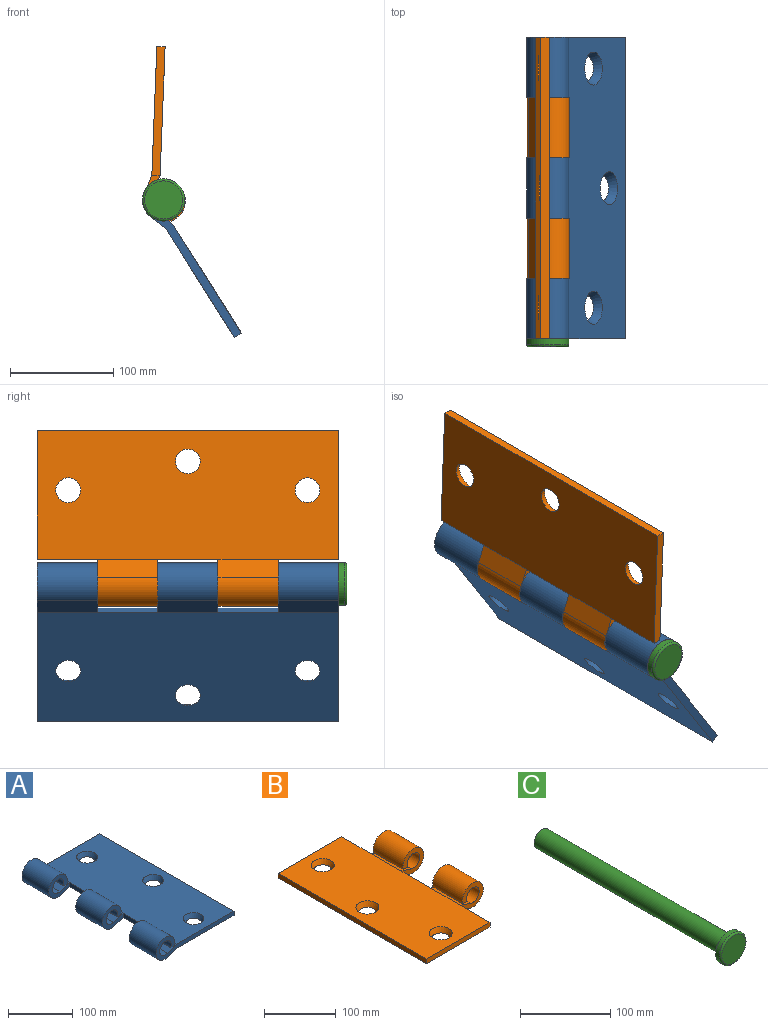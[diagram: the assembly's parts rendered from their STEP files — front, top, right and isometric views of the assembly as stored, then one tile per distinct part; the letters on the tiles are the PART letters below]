
ASSEMBLY  parts=3 mates=2
PART A: 29 faces, bbox 170x292x41 mm
  f0: cylinder r=12.5mm len=58.4mm, axis (0,1,0), area 3975.6mm2, adj f2,f8,f24,f28
  f1: cylinder r=12.5mm len=58.4mm, axis (0,1,0), area 3975.6mm2, adj f3,f9,f18,f25
  f2: plane 58.4x20.54mm, normal (-0.32,0,0.95), area 1264.7mm2, adj f0,f12,f24,f28
  f3: plane 58.4x20.54mm, normal (-0.32,0,0.95), area 1264.7mm2, adj f1,f12,f18,f25
  f4: plane 58.4x17.59mm, normal (0.34,0,-0.94), area 1091mm2, adj f6,f14,f24,f28
  f5: plane 58.4x17.59mm, normal (0.34,0,-0.94), area 1091mm2, adj f7,f14,f18,f25
  f6: cylinder r=20.5mm len=58.4mm, axis (0,1,0), area 6348.4mm2, adj f4,f8,f24,f28
  f7: cylinder r=20.5mm len=58.4mm, axis (0,1,0), area 6348.4mm2, adj f5,f9,f18,f25
  f8: plane 58.4x8.42mm, normal (0,0,-1), area 492mm2, adj f0,f6,f24,f28
  f9: plane 58.4x8.42mm, normal (0,0,-1), area 492mm2, adj f1,f7,f18,f25
  f10: cylinder r=12.5mm len=58.4mm, axis (0,1,0), area 3975.6mm2, adj f11,f17,f19,f27
  f11: plane 58.4x20.54mm, normal (-0.32,0,0.95), area 1264.7mm2, adj f10,f12,f19,f27
  f12: plane 292x125mm, normal (0,0,1), area 34087.3mm2, adj f2,f3,f11,f13,f18,f19,f20,f21
  f13: plane 292x8mm, normal (1,0,0), area 2336mm2, adj f12,f14,f18,f19
  f14: plane 292x125mm, normal (0,0,-1), area 35142.8mm2, adj f4,f5,f13,f15,f18,f19,f20,f21
  f15: plane 58.4x17.59mm, normal (0.34,0,-0.94), area 1091mm2, adj f14,f16,f19,f27
  f16: cylinder r=20.5mm len=58.4mm, axis (0,1,0), area 6348.4mm2, adj f15,f17,f19,f27
  f17: plane 58.4x8.42mm, normal (0,0,-1), area 492mm2, adj f10,f16,f19,f27
  f18: plane 170x41mm, normal (0,-1,0), area 1864mm2, adj f1,f3,f5,f7,f9,f12,f13,f14
  f19: plane 170x41mm, normal (0,1,0), area 1864mm2, adj f10,f11,f12,f13,f14,f15,f16,f17
  f20: cone r=12mm half-angle=26.6deg, axis (0,0,1), area 786.8mm2, adj f12,f14
  f21: cone r=12mm half-angle=26.6deg, axis (0,0,1), area 786.8mm2, adj f12,f14
  f22: cone r=12mm half-angle=26.6deg, axis (0,0,1), area 786.8mm2, adj f12,f14
  f23: plane 58.4x8mm, normal (-1,0,0), area 467.2mm2, adj f12,f14,f24,f25
  f24: plane 45x41mm, normal (0,-1,0), area 864mm2, adj f0,f2,f4,f6,f8,f23
  f25: plane 45x41mm, normal (0,1,0), area 864mm2, adj f1,f3,f5,f7,f9,f23
  f26: plane 58.4x8mm, normal (-1,0,0), area 467.2mm2, adj f12,f14,f27,f28
  f27: plane 45x41mm, normal (0,-1,0), area 864mm2, adj f10,f11,f15,f16,f17,f26
  f28: plane 45x41mm, normal (0,1,0), area 864mm2, adj f0,f2,f4,f6,f8,f26
PART B: 25 faces, bbox 170x292x41 mm
  f0: cylinder r=12.5mm len=58.4mm, axis (0,1,0), area 3975.6mm2, adj f2,f8,f21,f24
  f1: cylinder r=12.5mm len=58.4mm, axis (0,1,0), area 3975.6mm2, adj f3,f9,f19,f22
  f2: plane 58.4x20.54mm, normal (0.32,0,0.95), area 1264.7mm2, adj f0,f12,f21,f24
  f3: plane 58.4x20.54mm, normal (0.32,0,0.95), area 1264.7mm2, adj f1,f12,f19,f22
  f4: plane 58.4x17.59mm, normal (-0.34,0,-0.94), area 1091mm2, adj f6,f14,f21,f24
  f5: plane 58.4x17.59mm, normal (-0.34,0,-0.94), area 1091mm2, adj f7,f14,f19,f22
  f6: cylinder r=20.5mm len=58.4mm, axis (0,1,0), area 6348.4mm2, adj f4,f8,f21,f24
  f7: cylinder r=20.5mm len=58.4mm, axis (0,1,0), area 6348.4mm2, adj f5,f9,f19,f22
  f8: plane 58.4x8.42mm, normal (0,0,-1), area 492mm2, adj f0,f6,f21,f24
  f9: plane 58.4x8.42mm, normal (0,0,-1), area 492mm2, adj f1,f7,f19,f22
  f10: plane 125x8mm, normal (0,-1,0), area 1000mm2, adj f12,f13,f14,f18
  f11: plane 125x8mm, normal (0,1,0), area 1000mm2, adj f12,f13,f14,f23
  f12: plane 292x125mm, normal (0,0,1), area 34087.3mm2, adj f2,f3,f10,f11,f13,f15,f16,f17
  f13: plane 292x8mm, normal (-1,0,0), area 2336mm2, adj f10,f11,f12,f14
  f14: plane 292x125mm, normal (0,0,-1), area 35142.8mm2, adj f4,f5,f10,f11,f13,f15,f16,f17
  f15: cone r=12mm half-angle=26.6deg, axis (0,0,1), area 786.8mm2, adj f12,f14
  f16: cone r=12mm half-angle=26.6deg, axis (0,0,1), area 786.8mm2, adj f12,f14
  f17: cone r=12mm half-angle=26.6deg, axis (0,0,1), area 786.8mm2, adj f12,f14
  f18: plane 58.4x8mm, normal (1,0,0), area 467.2mm2, adj f10,f12,f14,f19
  f19: plane 45x41mm, normal (0,-1,0), area 864mm2, adj f1,f3,f5,f7,f9,f18
  f20: plane 58.4x8mm, normal (1,0,0), area 467.2mm2, adj f12,f14,f21,f22
  f21: plane 45x41mm, normal (0,-1,0), area 864mm2, adj f0,f2,f4,f6,f8,f20
  f22: plane 45x41mm, normal (0,1,0), area 864mm2, adj f1,f3,f5,f7,f9,f20
  f23: plane 58.4x8mm, normal (1,0,0), area 467.2mm2, adj f11,f12,f14,f24
  f24: plane 45x41mm, normal (0,1,0), area 864mm2, adj f0,f2,f4,f6,f8,f23
PART C: 6 faces, bbox 44.4x300x44.4 mm
  f0: cylinder r=12.25mm len=292mm, axis (0,-1,0), area 22475mm2, adj f1,f4
  f1: plane 24.5x24.5mm, normal (0,1,0), area 471.4mm2, adj f0
  f2: cylinder r=20.5mm len=41mm, axis (0,1,0), area 772.8mm2, adj f4,f5
  f3: plane 37x37mm, normal (0,-1,0), area 1075.2mm2, adj f5
  f4: plane 41x41mm, normal (0,1,0), area 848.8mm2, adj f0,f2
  f5: torus R=18.5mm, axis (0,-1,0), area 390.3mm2, adj f2,f3
PLACE A rot(axis=(0,1,0),57.8deg) t=(7.21,0,23.06)mm
PLACE B rot(axis=(0,1,0),92.2deg) t=(21.04,0,28.62)mm
PLACE C at identity fixed
MATE revolute A.f0 <-> B.f19  axis (0,1,0) through (24.5,-233.6,5)mm
MATE revolute A.f0 <-> C.f0  axis (0,1,0) through (24.5,-292,5)mm
